# Revit family: Airese Constant Flow Valve BIM file
name_source: partatom
category: Air Terminals
units: mm (PartAtom-declared; Revit-internal decimal feet)

## family parameters
Always vertical = Yes
Cut with Voids When Loaded = No
Part Type = Normal
Room Calculation Point = No
Round Connector Dimension = Use Diameter
Shared = No
Work Plane-Based = No

## types (11) — shared parameters
Acoustic power level Lw in dB(A) at 136 Pa = 32
Certification = -
Connection = Circular
Control = Manual
For ceiling mounting, a suitable connector is required = Yes
Manufacturer = Airflow Developments
Manufacturer URL Link = https://www.airflow.com
Material 1 = ANJ010012 1
Material 2 = ANJ010012 2
Max Flow = 8.3 L/s
Max. operating pressure (in Pa) = 160
Min Flow = 4.2 L/s
Minimum operating pressure (in Pa) = 50
NominalDepth = 40
NominalWidth = 170
Product URL link = https://www.airflow.com
Shape = Circular
Sleeve = Mandatory
Sound attenuation Dne, w (C) in db = 55
Testing reports = -
URL = https://www.airflow.com
zero-valued in all types: Default Elevation

## per-type parameters (varying)
| type | Model | Product name |
| 9041234 | Airese Constant Flow Valve 15m3/hr | Airese Constant Flow Valve 15m3/hr |
| 9041235 | Airese Constant Flow Valve 30m3/hr | Airese Constant Flow Valve 30m3/hr |
| 9041236 | Airese Pull Cord Boost Valve 15-30m3/h | Airese Pull Cord Boost Valve 15-30m3/h |
| 9041237 | Airese Pull Cord Boost Valve 15-75m3/h | Airese Pull Cord Boost Valve 15-75m3/h |
| 9041238 | Airese Humidity Boost Valve 15-45m3/h | Airese Humidity Boost Valve 15-45m3/h |
| 9041239 | Airese Humidity Boost Valve 10-45m3/h | Airese Humidity Boost Valve 10-45m3/h |
| 9041240 | Airese Valve Humidity Boost and Timer 12-105m3/hr | Airese Valve Humidity Boost and Timer 12-105m3/hr |
| 9041241 | Airese Humidity Boost Valve 5-100m3/hr | Airese Humidity Boost Valve 5-100m3/hr |
| 9041242 | Airese Pull Cord & Humidity Boost Valve 6m3/h - 40/90m3/hr | Airese Pull Cord & Humidity Boost Valve 6m3/h - 40/90m3/hr |
| 9041243 | Airese Electric Boost Valve 5-30m3/hr | Airese Electric Boost Valve 5-30m3/hr |
| 9041244 | Airese Electric Boost Valve 5-30m3/h | Airese Electric Boost Valve 5-30m3/h |

note: column(s) folded — value = type name in every type: Airflow part no

## geometry (parser evidence)
native form markers: Sweep x6
no freeform markers — native parametric forms only
